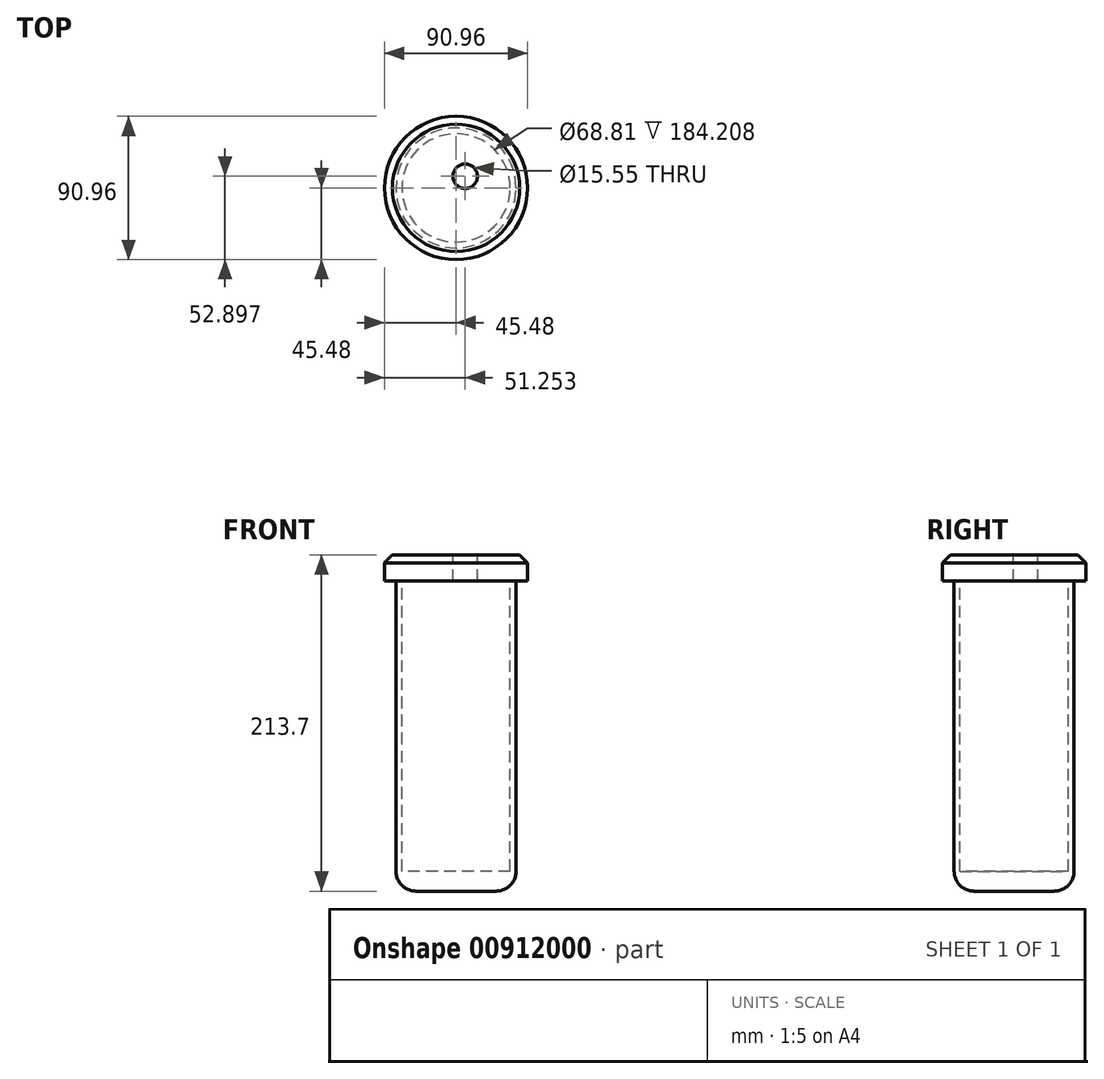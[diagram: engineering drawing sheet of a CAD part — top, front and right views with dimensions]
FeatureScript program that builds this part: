
annotation { "Feature Type Name" : "Feature", "Feature Type Description" : "" }
export const myFeature = defineFeature(function(context is Context, id is Id, definition is map)
    precondition{}
    {
        {
            var Q0;
            Q0=qCreatedBy(makeId("Right.planeOp"),FACE);
            var sketch = newSketch(context, id + "F0", { "sketchPlane" : qUnion([Q0])});
            skLineSegment(sketch, "E0", {"start": v(0, 0) * mm, "end": v(38.1, 0) * mm, "construction": true});
            skLineSegment(sketch, "E1", {"start": v(38.1, 0) * mm, "end": v(38.1, 101.6) * mm});
            skLineSegment(sketch, "E2", {"start": v(38.1, 0) * mm, "end": v(38.1, -101.6) * mm});
            skLineSegment(sketch, "E3", {"start": v(0, 0) * mm, "end": v(0, 101.6) * mm});
            skLineSegment(sketch, "E4", {"start": v(0, 0) * mm, "end": v(0, -101.6) * mm});
            skLineSegment(sketch, "E5", {"start": v(0, 101.6) * mm, "end": v(38.1, 101.6) * mm});
            skLineSegment(sketch, "E6", {"start": v(0, -101.6) * mm, "end": v(38.1, -101.6) * mm});
            skSolve(sketch);
        }
        {
            var Q0;
            Q0 = qSketchRegion(id + "F0", true);
            var Q1;
            Q1=sQuery(id+"F0.wireOp",EDGE,"E4");
            revolve(context, id + "F1", {"surfaceOperationType" : NewSurfaceOperationType.NEW, "entities" : qUnion([Q0]), "axis" : qUnion([Q1]), "revolveType" : RevolveType.FULL});
        }
        {
            var Q0;
            Q0=makeQuery(id+"F1.opRevolve","SWEPT_FACE",FACE,{"disambiguationData":[OSD([sQuery(id+"F0.wireOp",EDGE,"E5")])]});
            var sketch = newSketch(context, id + "F2", { "sketchPlane" : qUnion([Q0])});
            skCircle(sketch, "E7", {"center": v(0, 0) * mm, "radius": 34.4 * mm});
            skSolve(sketch);
        }
        {
            var Q0;
            Q0=makeQuery(id+"F2.imprint","IMPRINT",FACE,{"disambiguationData":[TD([[makeQuery(id+"F2.imprint","IMPRINT",EDGE,{"derivedFrom":sQuery(id+"F2.wireOp",EDGE,"E7")}),1.0]])]});
            extrude(context, id + "F3", {"entities" : qUnion([Q0]), "operationType" : NewBodyOperationType.REMOVE, "oppositeDirection" : true, "depth" : 190.5 * mm, "offsetDistance" : 25.4 * mm});
        }
        {
            var Q0;
            Q0=makeQuery(id+"F3.boolean.opBoolean","COPY",FACE,{"derivedFrom":makeQuery(id+"F3.opExtrude","CAP_FACE",FACE,{"disambiguationData":[OSD([sQuery(id+"F2.wireOp",EDGE,"E7")])],"isStart":false})});
            var sketch = newSketch(context, id + "F4", { "sketchPlane" : qUnion([Q0])});
            skCircle(sketch, "E8", {"center": v(5.7, 7.36) * mm, "radius": 6.7 * mm});
            skCircle(sketch, "E9", {"center": v(5.7, 7.36) * mm, "radius": 5.28 * mm});
            skSolve(sketch);
        }
        {
            var Q0;
            Q0=sQuery(id+"F4.wireOp",EDGE,"E8");
            extrude(context, id + "F5", {"bodyType" : ToolBodyType.SURFACE, "surfaceEntities" : qUnion([Q0]), "depth" : 240.8 * mm, "offsetDistance" : 25.4 * mm});
        }
        {
            var Q0;
            Q0=makeQuery(id+"F1.opRevolve","SWEPT_EDGE",EDGE,{"disambiguationData":[OSD([sQuery(id+"F0.wireOp",EDGE,"E2"),sQuery(id+"F0.wireOp",EDGE,"E6")])]});
            fillet(context, id + "F6", {"entities" : qUnion([Q0]), "radius" : 12.7 * mm, "tangentPropagation" : true, "allowEdgeOverflow" : false});
        }
        {
            var Q0;
            Q0=makeQuery(id+"F1.opRevolve","SWEPT_EDGE",EDGE,{"disambiguationData":[OSD([sQuery(id+"F0.wireOp",EDGE,"E1"),sQuery(id+"F0.wireOp",EDGE,"E5")])]});
            fillet(context, id + "F7", {"entities" : qUnion([Q0]), "radius" : 5.08 * mm, "tangentPropagation" : true, "allowEdgeOverflow" : false});
        }
        {
            var Q0;
            Q0=qCreatedBy(makeId("Right.planeOp"),FACE);
            var sketch = newSketch(context, id + "F8", { "sketchPlane" : qUnion([Q0])});
            skLineSegment(sketch, "E10", {"start": v(0, 112.1) * mm, "end": v(0, 95.3) * mm});
            skLineSegment(sketch, "E11", {"start": v(0, 95.3) * mm, "end": v(45.48, 95.3) * mm});
            skLineSegment(sketch, "E12", {"start": v(45.48, 95.3) * mm, "end": v(45.48, 112.1) * mm});
            skLineSegment(sketch, "E13", {"start": v(45.48, 112.1) * mm, "end": v(0, 112.1) * mm});
            skSolve(sketch);
        }
        {
            var Q0;
            Q0=makeQuery(id+"F8.imprint","IMPRINT",FACE,{"disambiguationData":[TD([[makeQuery(id+"F8.imprint","IMPRINT",EDGE,{"derivedFrom":sQuery(id+"F8.wireOp",EDGE,"E10")}),1.0]])]});
            var Q1;
            Q1=sQuery(id+"F8.wireOp",EDGE,"E10");
            revolve(context, id + "F9", {"operationType" : NewBodyOperationType.ADD, "surfaceOperationType" : NewSurfaceOperationType.NEW, "entities" : qUnion([Q0]), "axis" : qUnion([Q1]), "revolveType" : RevolveType.FULL});
        }
        {
            var Q0;
            Q0=makeQuery(id+"F9.opRevolve","SWEPT_FACE",FACE,{"disambiguationData":[OSD([sQuery(id+"F8.wireOp",EDGE,"E13")])]});
            var sketch = newSketch(context, id + "F10", { "sketchPlane" : qUnion([Q0])});
            skCircle(sketch, "E14", {"center": v(5.77, 7.42) * mm, "radius": 7.78 * mm});
            skSolve(sketch);
        }
        {
            var Q0;
            Q0=makeQuery(id+"F10.imprint","IMPRINT",FACE,{"disambiguationData":[TD([[makeQuery(id+"F10.imprint","IMPRINT",EDGE,{"derivedFrom":sQuery(id+"F10.wireOp",EDGE,"E14")}),1.0]])]});
            extrude(context, id + "F11", {"entities" : qUnion([Q0]), "operationType" : NewBodyOperationType.REMOVE, "oppositeDirection" : true, "depth" : 177.8 * mm, "offsetDistance" : 25.4 * mm});
        }
        {
            var Q0;
            Q0=makeQuery(id+"F9.opRevolve","SWEPT_EDGE",EDGE,{"disambiguationData":[OSD([sQuery(id+"F8.wireOp",EDGE,"E12"),sQuery(id+"F8.wireOp",EDGE,"E13")])]});
            chamfer(context, id + "F12", {"entities" : qUnion([Q0]), "width" : 5.08 * mm, "tangentPropagation" : true});
        }
    });
